# Revit family: Cisterns-ToiletCisterns-Vitra-S20Series-5514-003-0107
name_source: partatom
category: Plumbing Fixtures
revit_build: Autodesk Revit 2017 (Build: 20160225_1515(x64)
units: mm (PartAtom-declared; Revit-internal decimal feet)

## family parameters
Cut with Voids When Loaded = No
Host = Face
OmniClass Number = 23.45.05.21.11
OmniClass Title = Water Closets
Part Type = Normal
Room Calculation Point = No
Round Connector Dimension = Use Diameter
Shared = Yes

## types (1)
- WC_ToiletCisterns-Vitra_S20Series_5514-003-0107
    Article No. (default) = 5514-003-0107
    BIMobject category = Toilet Cisterns
    CW Connection = Yes
    Color = White
    Cost = 0 $
    Default Elevation = 410 mm  [stored 1.34514 ft]
    Description = VitrA S20  WC Cisterns
    Design country = Turkey
    HW Connection = No
    IFC Classification = Sanitary Terminal
    Main Material = Ceramic
    Manufacturer = Vitra
    Manufacturer name = Vitra
    Model = 5514-003-0107
    MountingType = WC Face Mounted
    NBS Referans Code = 35-93-90
    NBS Referans Description = Wc Cisterns
    Nominal Depth (mm) = 150 mm
    Nominal Height (mm) = 400 mm  [stored 1.31234 ft]
    Nominal Width (mm) = 400 mm  [stored 1.31234 ft]
    OmniClass Code = 23-31 19 19
    OmniClass Description = Water Closets
    Product SKU = 5514-003-0107
    Product certification = https://vitraglobal.com
    Product family = S20
    Product group = WC Cisterns
    Secondary Material = Ceramic-White
    URL = https://www.vitra.com.tr
    Uniclass 2.0 Code = PR-35-93-90
    Uniclass 2.0 Description = Wc Cisterns
    Uniclass 2015 Code = Pr_40_20_93_89
    Uniclass 2015 Name = WC cisterns
    Vent Connection = No
    Warranty Period (Year) = 10 Years
    Waste Connection = No
    Weight Net (kg) = 14,110
    Youtube = https://www.youtube.com

note: [stored X ft] marks values corroborated as IEEE doubles in the binary element streams (Revit-internal decimal feet)

## geometry (parser evidence)
native form markers: Sweep x3
no freeform markers — native parametric forms only
